# Revit family: OnSoft
name_source: partatom
category: Furniture
units: mm (PartAtom-declared; Revit-internal decimal feet)

## family parameters
Always vertical = Yes
Cut with Voids When Loaded = No
OmniClass Number = 23.40.20.00
OmniClass Title = General Furniture and Specialties
Room Calculation Point = No
Shared = No
Work Plane-Based = No

## types (4) — shared parameters
Depth = 465 mm  [stored 1.52559 ft]
Model = OnSoft
Surface finish = Porcelain
URL = www.hafa.se

## per-type parameters (varying)
| type | Art.No | GTIN | Width | Width ho |
| OnSoft600 | 1273160 | 7330027106946 | 610 mm  [stored 2.00131 ft] | 455 mm  [stored 1.49278 ft] |
| OnSoft800 | 1273161 | 7330027106953 | 810 mm | 503 mm  [stored 1.65026 ft] |
| OnSoft900 | 1273162 | 7330027106960 | 910 mm | 530 mm  [stored 1.73885 ft] |
| OnSoft1000 | 1273162 | 7330027106960 | 1010 mm  [stored 3.31365 ft] | 535 mm  [stored 1.75525 ft] |

note: [stored X ft] marks values corroborated as IEEE doubles in the binary element streams (Revit-internal decimal feet)

## geometry (parser evidence)
native form markers: Sweep x5
no freeform markers — native parametric forms only
